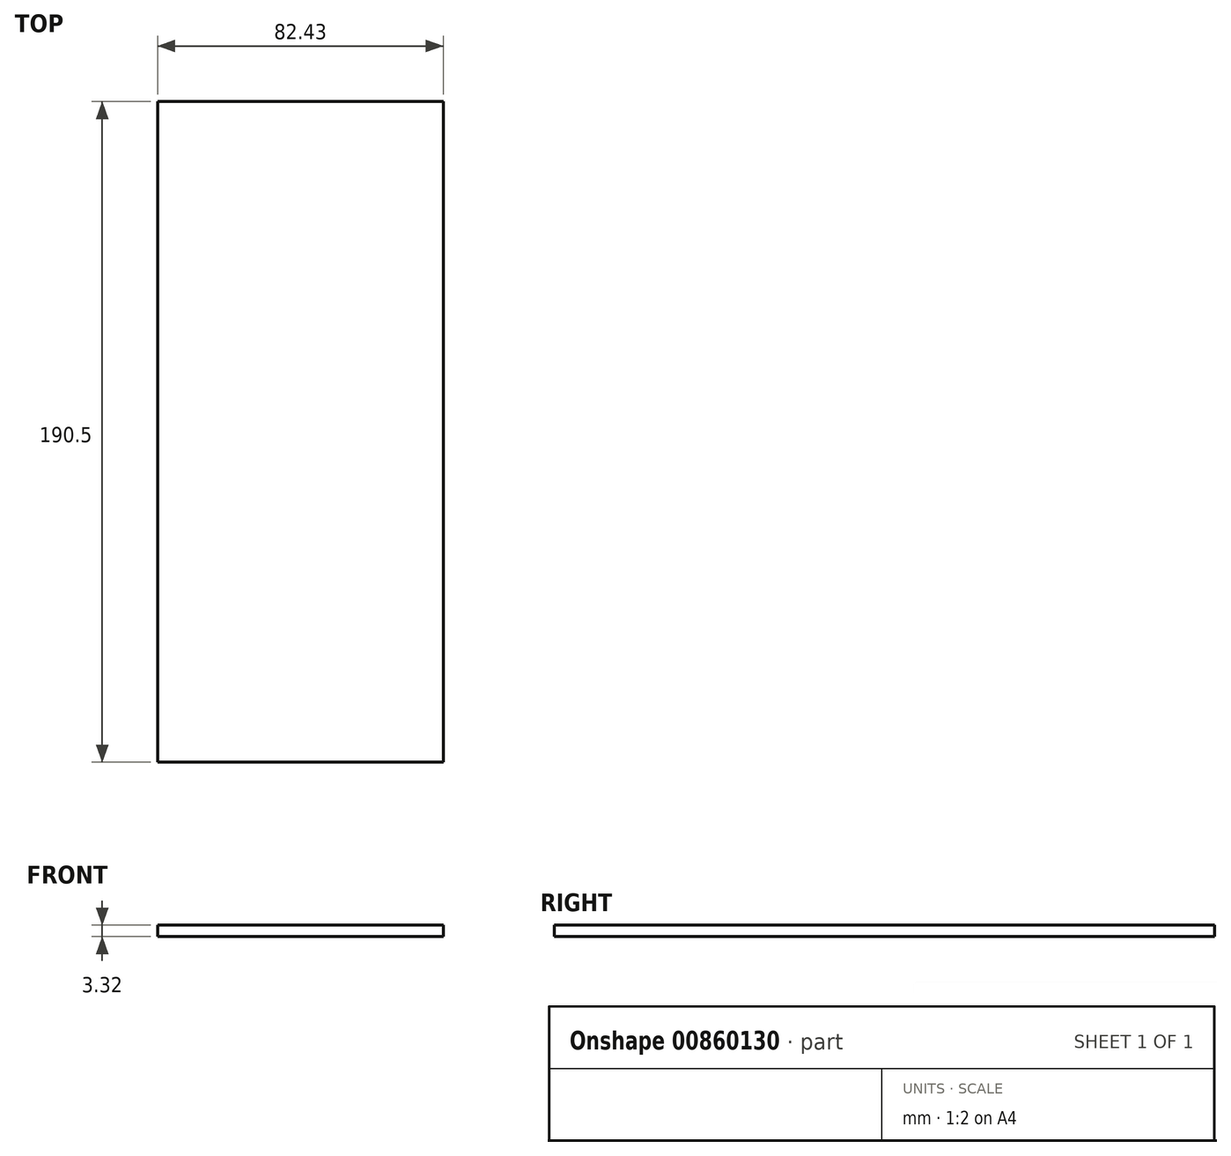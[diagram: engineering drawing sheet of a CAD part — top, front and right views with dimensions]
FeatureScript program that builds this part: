
annotation { "Feature Type Name" : "Feature", "Feature Type Description" : "" }
export const myFeature = defineFeature(function(context is Context, id is Id, definition is map)
    precondition{}
    {
        {
            var Q0;
            Q0=qCreatedBy(makeId("Front.planeOp"),FACE);
            var sketch = newSketch(context, id + "F0", { "sketchPlane" : qUnion([Q0])});
            skLineSegment(sketch, "E0.bottom", {"start": v(-21.29, 35.78) * mm, "end": v(61.14, 35.78) * mm});
            skLineSegment(sketch, "E0.top", {"start": v(-21.29, 32.46) * mm, "end": v(61.14, 32.46) * mm});
            skLineSegment(sketch, "E0.left", {"start": v(-21.29, 35.78) * mm, "end": v(-21.29, 32.46) * mm});
            skLineSegment(sketch, "E0.right", {"start": v(61.14, 35.78) * mm, "end": v(61.14, 32.46) * mm});
            skSolve(sketch);
        }
        {
            var Q0;
            Q0=sQuery(id+"F0.wireOp",EDGE,"E0.top");
            var Q1;
            Q1=sQuery(id+"F0.wireOp",EDGE,"E0.bottom");
            var Q2;
            Q2=sQuery(id+"F0.wireOp",EDGE,"E0.right");
            var Q3;
            Q3=sQuery(id+"F0.wireOp",EDGE,"E0.left");
            extrude(context, id + "F1", {"bodyType" : ToolBodyType.SURFACE, "surfaceEntities" : qUnion([Q0, Q1, Q2, Q3]), "depth" : 190.5 * mm, "offsetDistance" : 25.4 * mm});
        }
    });
